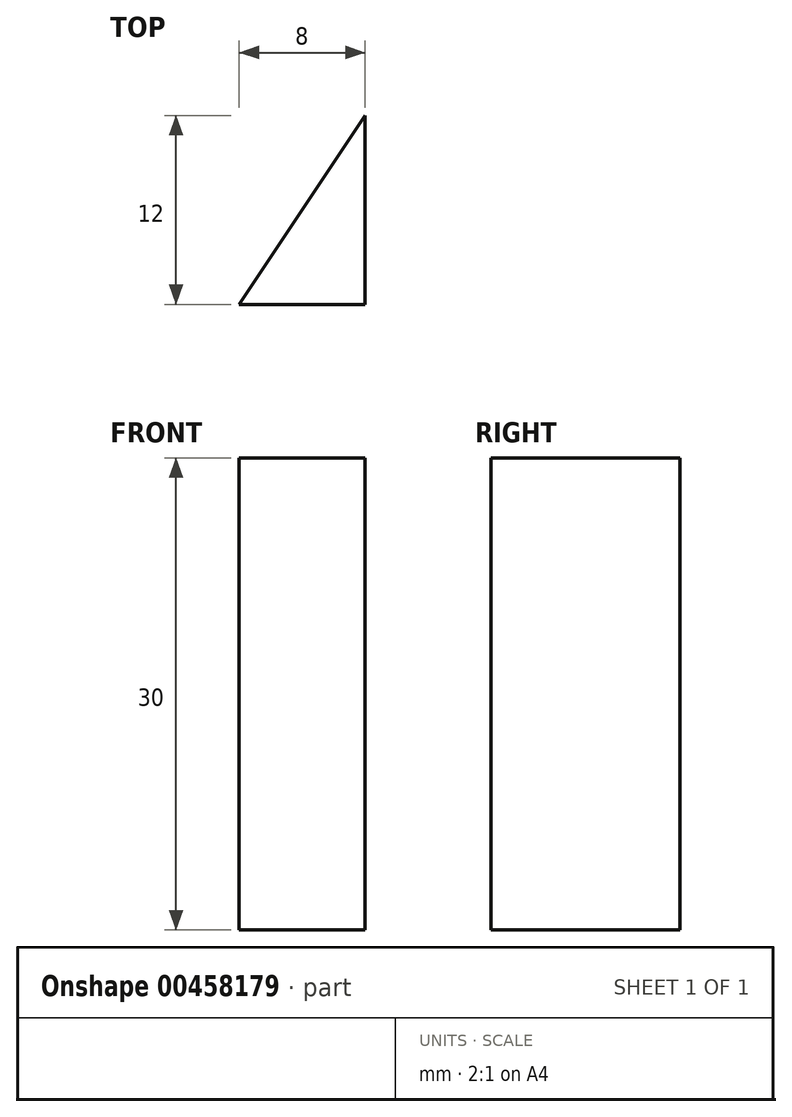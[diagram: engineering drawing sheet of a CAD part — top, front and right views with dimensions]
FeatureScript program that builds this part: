
annotation { "Feature Type Name" : "Feature", "Feature Type Description" : "" }
export const myFeature = defineFeature(function(context is Context, id is Id, definition is map)
    precondition{}
    {
        {
            var Q0;
            Q0=qCreatedBy(makeId("Top.planeOp"),FACE);
            var sketch = newSketch(context, id + "F0", { "sketchPlane" : qUnion([Q0])});
            skLineSegment(sketch, "E0", {"start": v(0, 0) * mm, "end": v(8, 0) * mm});
            skLineSegment(sketch, "E1", {"start": v(8, 0) * mm, "end": v(8, 12) * mm});
            skLineSegment(sketch, "E2", {"start": v(8, 12) * mm, "end": v(0, 0) * mm});
            skSolve(sketch);
        }
        {
            var Q0;
            Q0 = qSketchRegion(id + "F0", true);
            extrude(context, id + "F1", {"entities" : qUnion([Q0]), "depth" : 30 * mm});
        }
    });
